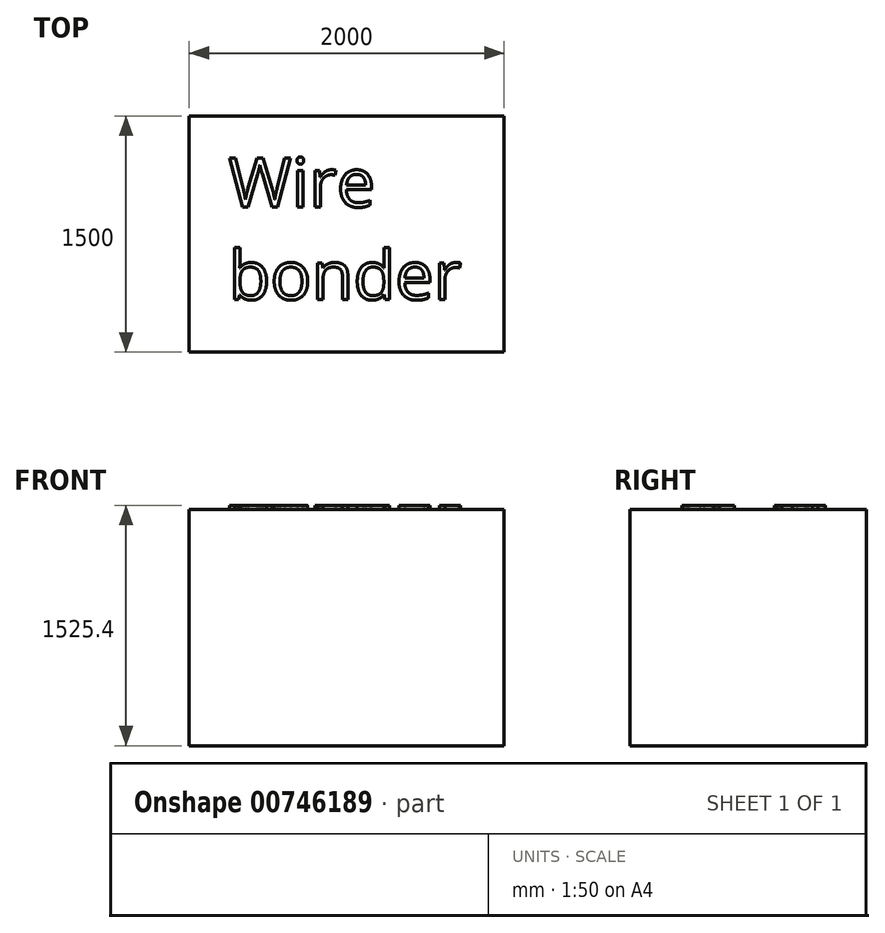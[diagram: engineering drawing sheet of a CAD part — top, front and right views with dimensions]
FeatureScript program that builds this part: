
annotation { "Feature Type Name" : "Feature", "Feature Type Description" : "" }
export const myFeature = defineFeature(function(context is Context, id is Id, definition is map)
    precondition{}
    {
        {
            var Q0;
            Q0=qCreatedBy(makeId("Top.planeOp"),FACE);
            var sketch = newSketch(context, id + "F0", { "sketchPlane" : qUnion([Q0])});
            skLineSegment(sketch, "E0.bottom", {"start": v(1000, -750) * mm, "end": v(-1000, -750) * mm});
            skLineSegment(sketch, "E0.top", {"start": v(1000, 750) * mm, "end": v(-1000, 750) * mm});
            skLineSegment(sketch, "E0.left", {"start": v(1000, -750) * mm, "end": v(1000, 750) * mm});
            skLineSegment(sketch, "E0.right", {"start": v(-1000, -750) * mm, "end": v(-1000, 750) * mm});
            skPoint(sketch, "E0.middle", {"position": v(0, 0) * mm});
            skSolve(sketch);
        }
        {
            var Q0;
            Q0=makeQuery(id+"F0.imprint","IMPRINT",FACE,{"disambiguationData":[TD([[makeQuery(id+"F0.imprint","IMPRINT",EDGE,{"derivedFrom":sQuery(id+"F0.wireOp",EDGE,"E0.bottom")}),-1.0]])]});
            extrude(context, id + "F1", {"entities" : qUnion([Q0]), "depth" : 1500 * mm, "offsetDistance" : 25.4 * mm});
        }
        {
            var Q0;
            Q0=makeQuery(id+"F1.opExtrude","CAP_FACE",FACE,{"disambiguationData":[OSD([sQuery(id+"F0.wireOp",EDGE,"E0.bottom"),sQuery(id+"F0.wireOp",EDGE,"E0.top"),sQuery(id+"F0.wireOp",EDGE,"E0.left"),sQuery(id+"F0.wireOp",EDGE,"E0.right")])],"isStart":false});
            var sketch = newSketch(context, id + "F2", { "sketchPlane" : qUnion([Q0])});
            skText(sketch, "E1", { "text": "Wire \nbonder\n", "fontName": "OpenSans-Regular.ttf"});
            const initialGuessF2  = {"E1": [-0.75, 0.1719, 1, 0, 0.31183]};
            skSetInitialGuess(sketch, initialGuessF2);
            skSolve(sketch);
        }
        {
            var Q0;
            Q0 = qSketchRegion(id + "F2", true);
            extrude(context, id + "F3", {"entities" : qUnion([Q0]), "operationType" : NewBodyOperationType.ADD, "depth" : 25.4 * mm, "offsetDistance" : 25.4 * mm});
        }
    });
